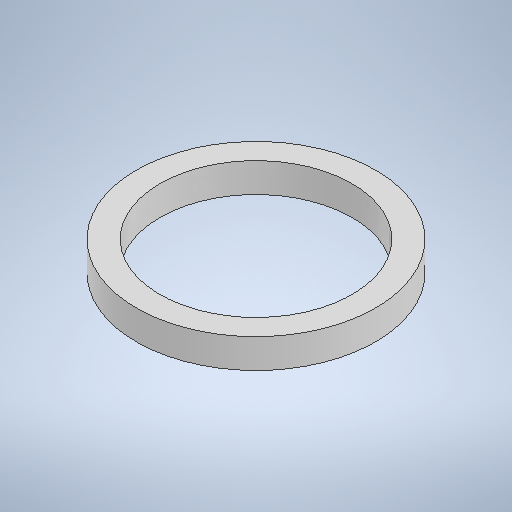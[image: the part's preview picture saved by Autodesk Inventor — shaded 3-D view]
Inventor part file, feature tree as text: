
AUTODESK INVENTOR PART (.ipt)
format: ipt  version: 2025 (Build 290162010, 162A)  size: 255,488 bytes
history: native  units: in
note: dims shown in document units (in); Inventor stores cm internally (conversion verified against a paired STEP export)
features: extrude x1, sketch x1
ambient origin geometry x8: Origin, YZ Plane, XZ Plane, XY Plane, X Axis, Y Axis, Z Axis, Center Point
bodies: Volumenkörper1 (feature_tree)
feature tree (2):
  extrude  "Extrusion1"  Depth=0.1969in
  sketch  "Skizze1"  dims[d0=1.6043in d1=0.1575in d2=0.1969in d3=0.0in]
